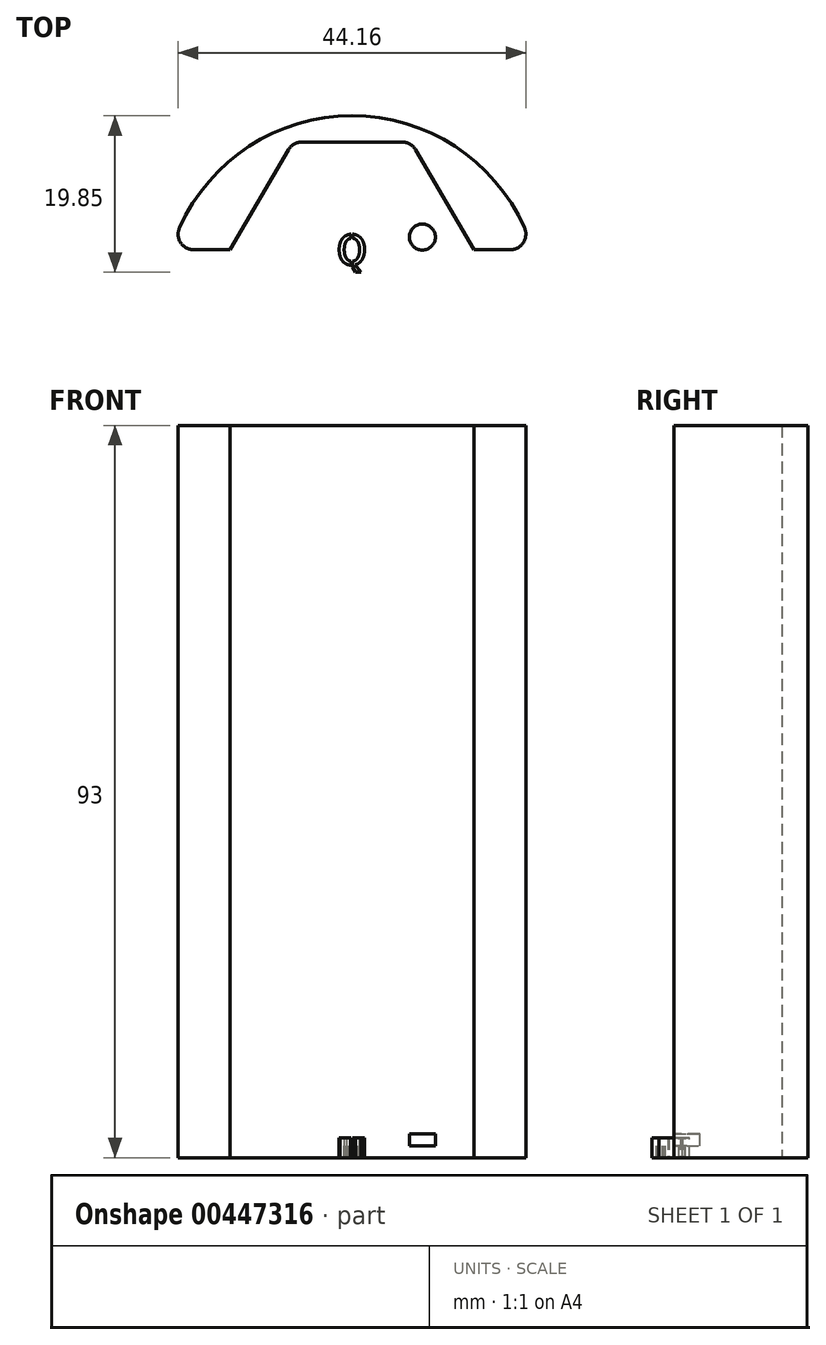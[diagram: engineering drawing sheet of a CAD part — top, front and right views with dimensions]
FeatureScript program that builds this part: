
annotation { "Feature Type Name" : "Feature", "Feature Type Description" : "" }
export const myFeature = defineFeature(function(context is Context, id is Id, definition is map)
    precondition{}
    {
        {
            var Q0;
            Q0=qCreatedBy(makeId("Top.planeOp"),FACE);
            var sketch = newSketch(context, id + "F0", { "sketchPlane" : qUnion([Q0])});
            skLineSegment(sketch, "E0", {"start": v(-15.5, -13.7) * mm, "end": v(-8.08, -1) * mm});
            skLineSegment(sketch, "E1", {"start": v(-6.35, 0) * mm, "end": v(6.35, 0) * mm});
            skLineSegment(sketch, "E2", {"start": v(8.08, -1) * mm, "end": v(15.5, -13.7) * mm});
            skLineSegment(sketch, "E3", {"start": v(-15.5, -13.7) * mm, "end": v(15.5, -13.7) * mm, "construction": true});
            skPoint(sketch, "E4", {"position": v(0, 0) * mm});
            skPoint(sketch, "E5", {"position": v(0, -13.7) * mm});
            skLineSegment(sketch, "E6", {"start": v(-15.5, -13.7) * mm, "end": v(-20.08, -13.7) * mm});
            skLineSegment(sketch, "E7", {"start": v(15.5, -13.7) * mm, "end": v(20.08, -13.7) * mm});
            skArc(sketch, "E8", {"start": v(21.9, -10.88) * mm, "mid": v(0, 3.32) * mm, "end": v(-21.9, -10.88) * mm});
            skPoint(sketch, "E9.visualSharp", {"position": v(-7.5, 0) * mm});
            skArc(sketch, "E9.filletArc", {"start": v(-6.35, 0) * mm, "mid": v(-7.35, -0.27) * mm, "end": v(-8.08, -1) * mm});
            skPoint(sketch, "E10.visualSharp", {"position": v(7.5, 0) * mm});
            skArc(sketch, "E10.filletArc", {"start": v(8.08, -1) * mm, "mid": v(7.35, -0.27) * mm, "end": v(6.35, 0) * mm});
            skPoint(sketch, "E11.visualSharp", {"position": v(-22.96, -13.7) * mm});
            skArc(sketch, "E11.filletArc", {"start": v(-21.9, -10.88) * mm, "mid": v(-21.76, -12.79) * mm, "end": v(-20.08, -13.7) * mm});
            skPoint(sketch, "E12.visualSharp", {"position": v(22.96, -13.7) * mm});
            skArc(sketch, "E12.filletArc", {"start": v(20.08, -13.7) * mm, "mid": v(21.76, -12.79) * mm, "end": v(21.9, -10.88) * mm});
            skSolve(sketch);
        }
        {
            var Q0;
            Q0=makeQuery(id+"F0.imprint","IMPRINT",FACE,{"disambiguationData":[TD([[makeQuery(id+"F0.imprint","IMPRINT",EDGE,{"derivedFrom":sQuery(id+"F0.wireOp",EDGE,"E0")}),1.0]])]});
            extrude(context, id + "F1", {"entities" : qUnion([Q0]), "depth" : 90 * mm});
        }
        {
            var Q0;
            Q0=makeQuery(id+"F1.opExtrude","CAP_FACE",FACE,{"disambiguationData":[OSD([sQuery(id+"F0.wireOp",EDGE,"E0"),sQuery(id+"F0.wireOp",EDGE,"E1"),sQuery(id+"F0.wireOp",EDGE,"E2"),sQuery(id+"F0.wireOp",EDGE,"E6"),sQuery(id+"F0.wireOp",EDGE,"E7"),sQuery(id+"F0.wireOp",EDGE,"E8"),sQuery(id+"F0.wireOp",EDGE,"E9.filletArc"),sQuery(id+"F0.wireOp",EDGE,"E10.filletArc")])],"isStart":true});
            var sketch = newSketch(context, id + "F2", { "sketchPlane" : qUnion([Q0])});
            skLineSegment(sketch, "E13", {"start": v(-17.96, 17.7) * mm, "end": v(17.96, 17.7) * mm});
            skArc(sketch, "E14", {"start": v(21.06, -6.01) * mm, "mid": v(0, -13.32) * mm, "end": v(-21.06, -6.01) * mm});
            skLineSegment(sketch, "E15", {"start": v(-22.96, -2.09) * mm, "end": v(-22.96, 12.7) * mm});
            skLineSegment(sketch, "E16", {"start": v(22.96, -2.09) * mm, "end": v(22.96, 12.7) * mm});
            skPoint(sketch, "E17.visualSharp", {"position": v(-22.96, 17.7) * mm});
            skArc(sketch, "E17.filletArc", {"start": v(-17.96, 17.7) * mm, "mid": v(-21.5, 16.24) * mm, "end": v(-22.96, 12.7) * mm});
            skPoint(sketch, "E18.visualSharp", {"position": v(22.96, 17.7) * mm});
            skArc(sketch, "E18.filletArc", {"start": v(22.96, 12.7) * mm, "mid": v(21.5, 16.24) * mm, "end": v(17.96, 17.7) * mm});
            skPoint(sketch, "E19.visualSharp", {"position": v(22.96, -4.4) * mm});
            skArc(sketch, "E19.filletArc", {"start": v(21.06, -6.01) * mm, "mid": v(22.46, -4.27) * mm, "end": v(22.96, -2.09) * mm});
            skPoint(sketch, "E20.visualSharp", {"position": v(-22.96, -4.4) * mm});
            skArc(sketch, "E20.filletArc", {"start": v(-22.96, -2.09) * mm, "mid": v(-22.46, -4.27) * mm, "end": v(-21.06, -6.01) * mm});
            skSolve(sketch);
        }
        {
            var Q0;
            Q0=makeQuery(id+"F2.imprint","IMPRINT",FACE,{"disambiguationData":[TD([[makeQuery(id+"F2.imprint","IMPRINT",EDGE,{"derivedFrom":sQuery(id+"F2.wireOp",EDGE,"E13")}),-1.0]])]});
            var Q1;
            Q1=makeQuery(id+"F0.imprint","IMPRINT",FACE,{"disambiguationData":[TD([[makeQuery(id+"F0.imprint","IMPRINT",EDGE,{"derivedFrom":sQuery(id+"F0.wireOp",EDGE,"E0")}),1.0]])]});
            extrude(context, id + "F3", {"entities" : qUnion([Q0, Q1]), "operationType" : NewBodyOperationType.ADD, "depth" : 3 * mm});
        }
        {
            var Q0;
            {var subQ0=sQuery(id+"F0.wireOp",EDGE,"E12.filletArc");var subQ1=sQuery(id+"F0.wireOp",EDGE,"E11.filletArc");var subQ2=sQuery(id+"F0.wireOp",EDGE,"E10.filletArc");var subQ3=sQuery(id+"F0.wireOp",EDGE,"E9.filletArc");var subQ4=sQuery(id+"F0.wireOp",EDGE,"E8");var subQ5=sQuery(id+"F0.wireOp",EDGE,"E7");var subQ6=sQuery(id+"F0.wireOp",EDGE,"E6");var subQ7=sQuery(id+"F0.wireOp",EDGE,"E2");var subQ8=sQuery(id+"F0.wireOp",EDGE,"E1");var subQ9=sQuery(id+"F0.wireOp",EDGE,"E0");Q0=makeQuery(id+"F3.boolean.opBoolean","MERGE",FACE,{"derivedFrom":[makeQuery(id+"F3.opExtrude","CAP_FACE",FACE,{"disambiguationData":[OSD([subQ9,subQ8,subQ7,subQ6,subQ5,subQ4,subQ3,subQ2,subQ1,subQ0])],"isStart":true}),makeQuery(id+"F3.opExtrude","CAP_FACE",FACE,{"disambiguationData":[OSD([subQ9,subQ8,subQ7,subQ6,subQ5,subQ4,subQ3,subQ2,subQ1,subQ0,sQuery(id+"F2.wireOp",EDGE,"E13"),sQuery(id+"F2.wireOp",EDGE,"E14"),sQuery(id+"F2.wireOp",EDGE,"a6c4aa1a-b442-44ca-937c-f53565c4f402.filletArc"),sQuery(id+"F2.wireOp",EDGE,"8f3339f9-6e3e-4ccb-8717-b49554667e36.filletArc")])],"isStart":true})]});}
            var sketch = newSketch(context, id + "F4", { "sketchPlane" : qUnion([Q0])});
            skCircle(sketch, "E21", {"center": v(0, -4.85) * mm, "radius": 1.65 * mm});
            skCircle(sketch, "E22", {"center": v(-8.94, -12.08) * mm, "radius": 1.65 * mm});
            skCircle(sketch, "E23.MirrorC", {"center": v(8.94, -12.08) * mm, "radius": 1.65 * mm});
            skText(sketch, "E24", { "text": "Q", "fontName": "AllertaStencil-Regular.ttf"});
            skPoint(sketch, "E25", {"position": v(0, -13.7) * mm});
            const initialGuessF4  = {"E24": [-0.00196, -0.01564, 1, 0, 0.00387]};
            skSetInitialGuess(sketch, initialGuessF4);
            skSolve(sketch);
        }
        {
            var Q0;
            Q0=makeQuery(id+"F4.imprint","IMPRINT",FACE,{"disambiguationData":[TD([[makeQuery(id+"F4.imprint","IMPRINT",EDGE,{"derivedFrom":sQuery(id+"F4.wireOp",EDGE,"E22")}),1.0]])]});
            var Q1;
            Q1=makeQuery(id+"F4.imprint","IMPRINT",FACE,{"disambiguationData":[TD([[makeQuery(id+"F4.imprint","IMPRINT",EDGE,{"derivedFrom":sQuery(id+"F4.wireOp",EDGE,"E21")}),1.0]])]});
            var Q2;
            Q2=makeQuery(id+"F4.imprint","IMPRINT",FACE,{"disambiguationData":[TD([[makeQuery(id+"F4.imprint","IMPRINT",EDGE,{"derivedFrom":sQuery(id+"F4.wireOp",EDGE,"E23.MirrorC")}),-1.0]])]});
            var Q3;
            {var subQ0=sQuery(id+"F0.wireOp",EDGE,"E12.filletArc");var subQ1=sQuery(id+"F0.wireOp",EDGE,"E11.filletArc");var subQ2=sQuery(id+"F0.wireOp",EDGE,"E10.filletArc");var subQ3=sQuery(id+"F0.wireOp",EDGE,"E9.filletArc");var subQ4=sQuery(id+"F0.wireOp",EDGE,"E8");var subQ5=sQuery(id+"F0.wireOp",EDGE,"E7");var subQ6=sQuery(id+"F0.wireOp",EDGE,"E6");var subQ7=sQuery(id+"F0.wireOp",EDGE,"E2");var subQ8=sQuery(id+"F0.wireOp",EDGE,"E1");var subQ9=sQuery(id+"F0.wireOp",EDGE,"E0");Q3=makeQuery(id+"F3.boolean.opBoolean","MERGE",FACE,{"derivedFrom":[makeQuery(id+"F3.opExtrude","CAP_FACE",FACE,{"disambiguationData":[OSD([subQ9,subQ8,subQ7,subQ6,subQ5,subQ4,subQ3,subQ2,subQ1,subQ0])],"isStart":false}),makeQuery(id+"F3.opExtrude","CAP_FACE",FACE,{"disambiguationData":[OSD([subQ9,subQ8,subQ7,subQ6,subQ5,subQ4,subQ3,subQ2,subQ1,subQ0,sQuery(id+"F2.wireOp",EDGE,"E13"),sQuery(id+"F2.wireOp",EDGE,"E14"),sQuery(id+"F2.wireOp",EDGE,"a6c4aa1a-b442-44ca-937c-f53565c4f402.filletArc"),sQuery(id+"F2.wireOp",EDGE,"8f3339f9-6e3e-4ccb-8717-b49554667e36.filletArc")])],"isStart":false})]});}
            extrude(context, id + "F5", {"entities" : qUnion([Q0, Q1, Q2]), "operationType" : NewBodyOperationType.REMOVE, "endBound" : BoundingType.UP_TO_SURFACE, "oppositeDirection" : true, "endBoundEntityFace" : qUnion([Q3]), "depth" : 25 * mm});
        }
        {
            var Q0;
            Q0=makeQuery(id+"F4.imprint","IMPRINT",FACE,{"disambiguationData":[TD([[makeQuery(id+"F4.imprint","IMPRINT",EDGE,{"derivedFrom":sQuery(id+"F4.wireOp",EDGE,"E24.sketch_text.stroke-0")}),-1.0]])]});
            var Q1;
            Q1=makeQuery(id+"F4.imprint","IMPRINT",FACE,{"disambiguationData":[TD([[makeQuery(id+"F4.imprint","IMPRINT",EDGE,{"derivedFrom":sQuery(id+"F4.wireOp",EDGE,"E24.sketch_text.stroke-19")}),-1.0]])]});
            extrude(context, id + "F6", {"entities" : qUnion([Q0, Q1]), "operationType" : NewBodyOperationType.REMOVE, "oppositeDirection" : true, "depth" : 0.5 * mm});
        }
        {
            var Q0;
            {var subQ0=sQuery(id+"F0.wireOp",EDGE,"E12.filletArc");var subQ1=sQuery(id+"F0.wireOp",EDGE,"E11.filletArc");var subQ2=sQuery(id+"F0.wireOp",EDGE,"E10.filletArc");var subQ3=sQuery(id+"F0.wireOp",EDGE,"E9.filletArc");var subQ4=sQuery(id+"F0.wireOp",EDGE,"E8");var subQ5=sQuery(id+"F0.wireOp",EDGE,"E7");var subQ6=sQuery(id+"F0.wireOp",EDGE,"E6");var subQ7=sQuery(id+"F0.wireOp",EDGE,"E2");var subQ8=sQuery(id+"F0.wireOp",EDGE,"E1");var subQ9=sQuery(id+"F0.wireOp",EDGE,"E0");Q0=makeQuery(id+"F3.boolean.opBoolean","MERGE",FACE,{"derivedFrom":[makeQuery(id+"F3.opExtrude","CAP_FACE",FACE,{"disambiguationData":[OSD([subQ9,subQ8,subQ7,subQ6,subQ5,subQ4,subQ3,subQ2,subQ1,subQ0])],"isStart":false}),makeQuery(id+"F3.opExtrude","CAP_FACE",FACE,{"disambiguationData":[OSD([subQ9,subQ8,subQ7,subQ6,subQ5,subQ4,subQ3,subQ2,subQ1,subQ0,sQuery(id+"F2.wireOp",EDGE,"E13"),sQuery(id+"F2.wireOp",EDGE,"E14"),sQuery(id+"F2.wireOp",EDGE,"a6c4aa1a-b442-44ca-937c-f53565c4f402.filletArc"),sQuery(id+"F2.wireOp",EDGE,"8f3339f9-6e3e-4ccb-8717-b49554667e36.filletArc")])],"isStart":false})]});}
            var sketch = newSketch(context, id + "F7", { "sketchPlane" : qUnion([Q0])});
            skCircle(sketch, "E26", {"center": v(-8.94, 12.08) * mm, "radius": 2.9 * mm});
            skCircle(sketch, "E27", {"center": v(0, 4.85) * mm, "radius": 2.9 * mm});
            skCircle(sketch, "E28", {"center": v(8.94, 12.08) * mm, "radius": 2.9 * mm});
            skSolve(sketch);
        }
        {
            var Q0;
            Q0=qSketchRegion(id+"F7",true);
            extrude(context, id + "F8", {"entities" : qUnion([Q0]), "operationType" : NewBodyOperationType.REMOVE, "oppositeDirection" : true, "depth" : 1.5 * mm});
        }
    });
